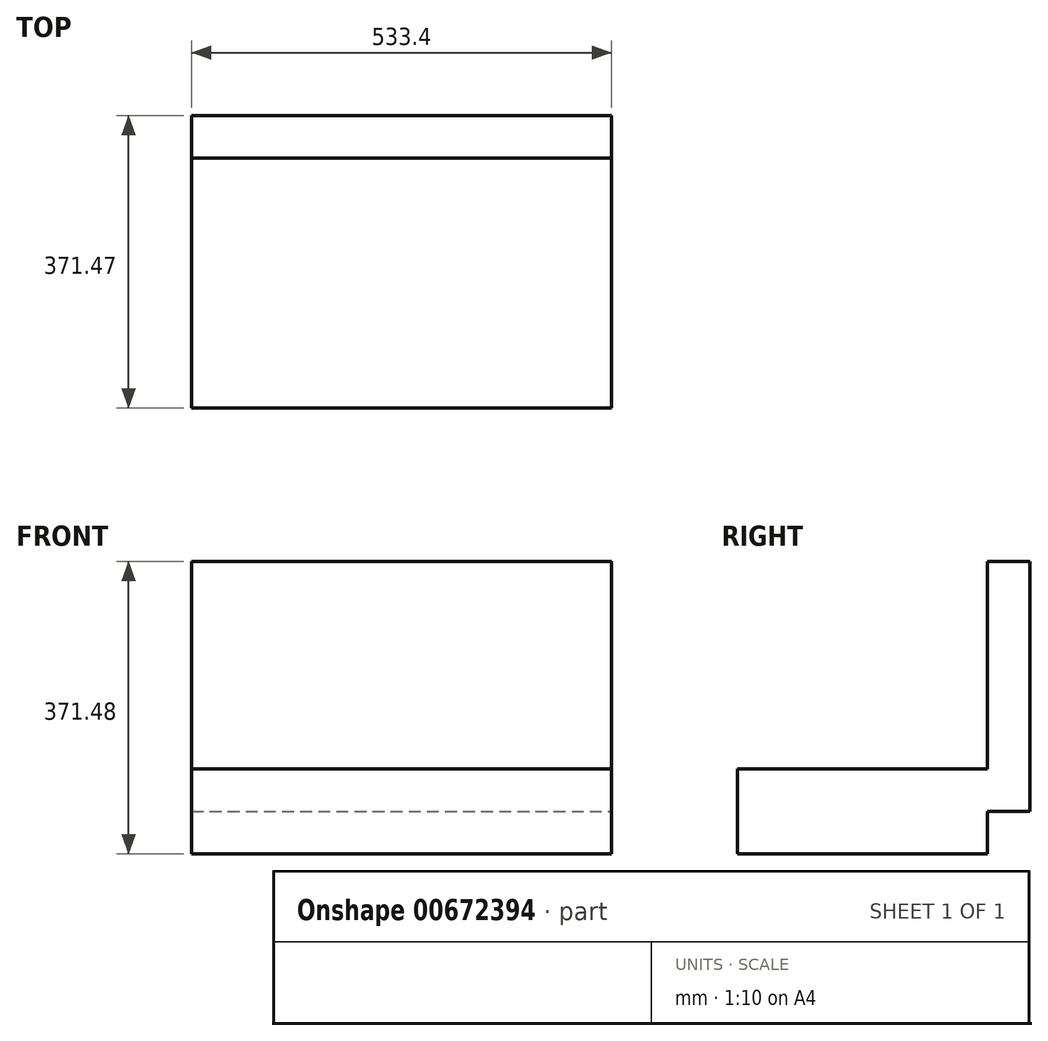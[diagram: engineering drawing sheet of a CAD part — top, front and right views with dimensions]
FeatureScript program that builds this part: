
annotation { "Feature Type Name" : "Feature", "Feature Type Description" : "" }
export const myFeature = defineFeature(function(context is Context, id is Id, definition is map)
    precondition{}
    {
        {
            var Q0;
            Q0=qCreatedBy(makeId("Top.planeOp"),FACE);
            var sketch = newSketch(context, id + "F0", { "sketchPlane" : qUnion([Q0])});
            skLineSegment(sketch, "E0.bottom", {"start": v(266.7, 158.75) * mm, "end": v(-266.7, 158.75) * mm});
            skLineSegment(sketch, "E0.top", {"start": v(266.7, -158.75) * mm, "end": v(-266.7, -158.75) * mm});
            skLineSegment(sketch, "E0.left", {"start": v(266.7, 158.75) * mm, "end": v(266.7, -158.75) * mm});
            skLineSegment(sketch, "E0.right", {"start": v(-266.7, 158.75) * mm, "end": v(-266.7, -158.75) * mm});
            skPoint(sketch, "E0.middle", {"position": v(0, 0) * mm});
            skSolve(sketch);
        }
        {
            var Q0;
            Q0 = qSketchRegion(id + "F0", true);
            extrude(context, id + "F1", {"entities" : qUnion([Q0]), "endBound" : BoundingType.SYMMETRIC, "depth" : 107.95 * mm, "offsetDistance" : 25.4 * mm});
        }
        {
            var Q0;
            Q0=qCreatedBy(makeId("Top.planeOp"),FACE);
            var sketch = newSketch(context, id + "F2", { "sketchPlane" : qUnion([Q0])});
            skLineSegment(sketch, "E1.bottom", {"start": v(-266.7, 212.72) * mm, "end": v(266.7, 212.72) * mm});
            skLineSegment(sketch, "E1.top", {"start": v(-266.7, 158.75) * mm, "end": v(266.7, 158.75) * mm});
            skLineSegment(sketch, "E1.left", {"start": v(-266.7, 212.72) * mm, "end": v(-266.7, 158.75) * mm});
            skLineSegment(sketch, "E1.right", {"start": v(266.7, 212.72) * mm, "end": v(266.7, 158.75) * mm});
            skPoint(sketch, "E1.middle", {"position": v(0, 196.97) * mm});
            skSolve(sketch);
        }
        {
            var Q0;
            Q0 = qSketchRegion(id + "F2", true);
            extrude(context, id + "F3", {"entities" : qUnion([Q0]), "operationType" : NewBodyOperationType.ADD, "depth" : 317.5 * mm, "offsetDistance" : 25.4 * mm});
        }
    });
